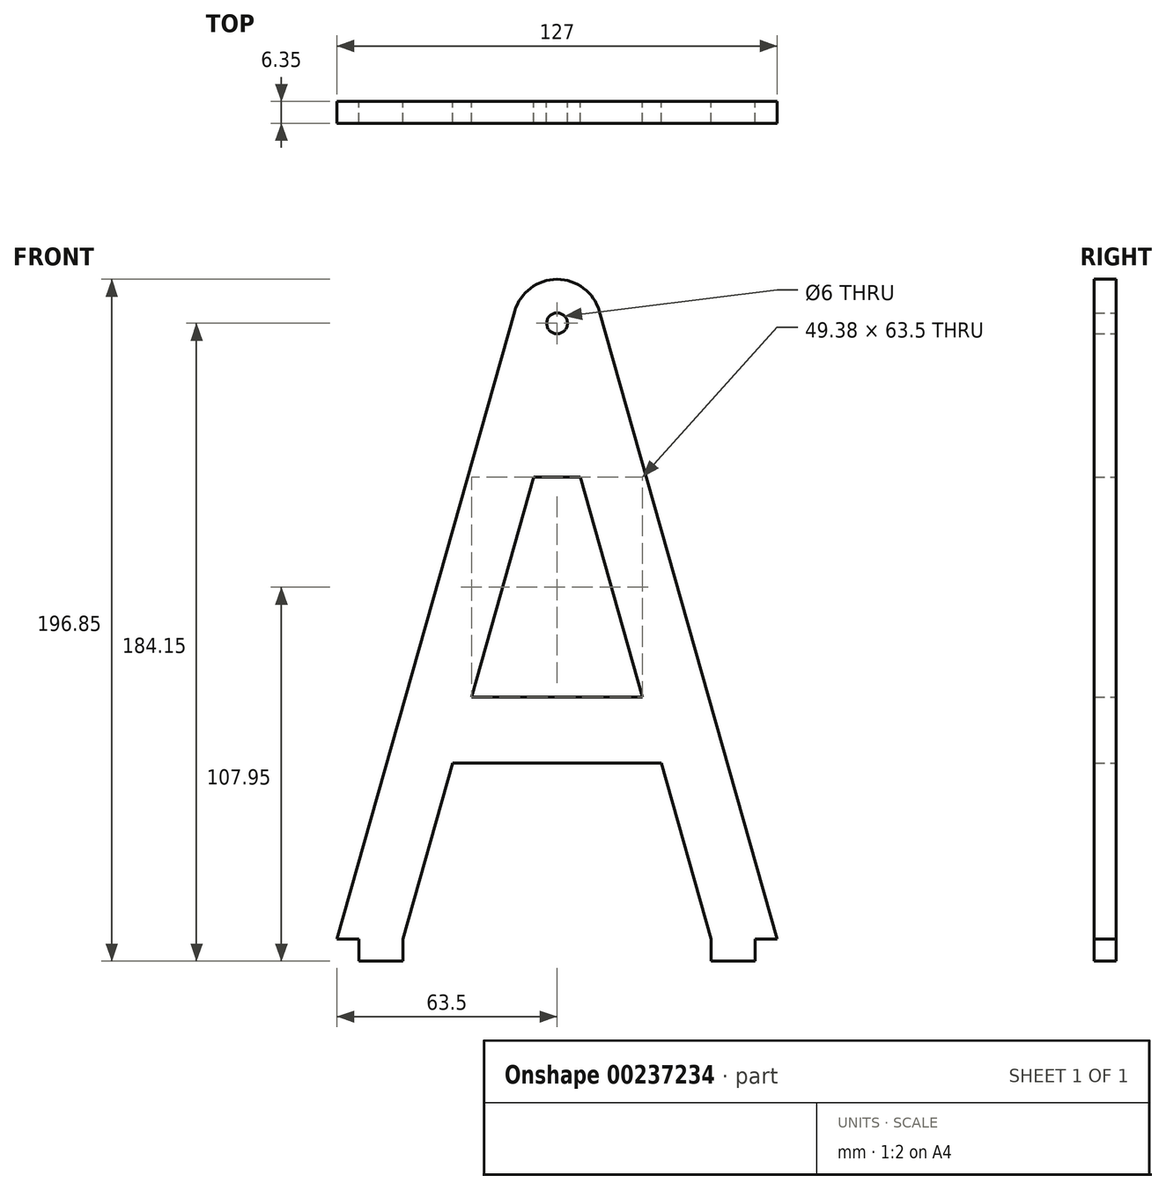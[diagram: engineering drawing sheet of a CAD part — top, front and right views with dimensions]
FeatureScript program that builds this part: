
annotation { "Feature Type Name" : "Feature", "Feature Type Description" : "" }
export const myFeature = defineFeature(function(context is Context, id is Id, definition is map)
    precondition{}
    {
        {
            var Q0;
            Q0=qCreatedBy(makeId("Front.planeOp"),FACE);
            var sketch = newSketch(context, id + "F0", { "sketchPlane" : qUnion([Q0])});
            skCircle(sketch, "E0", {"center": v(0, 177.8) * mm, "radius": 3 * mm});
            skArc(sketch, "E1", {"start": v(12.22, 181.26) * mm, "mid": v(0, 190.5) * mm, "end": v(-12.22, 181.26) * mm});
            skLineSegment(sketch, "E2", {"start": v(-12.22, 181.26) * mm, "end": v(-63.5, 0) * mm});
            skLineSegment(sketch, "E3", {"start": v(-63.5, 0) * mm, "end": v(-44.45, 0) * mm});
            skLineSegment(sketch, "E4", {"start": v(44.45, 0) * mm, "end": v(63.5, 0) * mm});
            skLineSegment(sketch, "E5", {"start": v(63.5, 0) * mm, "end": v(12.22, 181.26) * mm});
            skLineSegment(sketch, "E6", {"start": v(-30.08, 50.8) * mm, "end": v(30.08, 50.8) * mm});
            skLineSegment(sketch, "E7", {"start": v(30.08, 50.8) * mm, "end": v(44.45, 0) * mm});
            skLineSegment(sketch, "E8", {"start": v(-30.08, 50.8) * mm, "end": v(-44.45, 0) * mm});
            skLineSegment(sketch, "E9", {"start": v(-24.69, 69.85) * mm, "end": v(24.69, 69.85) * mm});
            skLineSegment(sketch, "E10", {"start": v(24.69, 69.85) * mm, "end": v(6.72, 133.35) * mm});
            skLineSegment(sketch, "E11", {"start": v(6.72, 133.35) * mm, "end": v(-6.72, 133.35) * mm});
            skLineSegment(sketch, "E12", {"start": v(-6.72, 133.35) * mm, "end": v(-24.69, 69.85) * mm});
            skSolve(sketch);
        }
        {
            var Q0;
            Q0 = qSketchRegion(id + "F0", true);
            extrude(context, id + "F1", {"entities" : qUnion([Q0]), "depth" : 6.35 * mm});
        }
        {
            var Q0;
            Q0=makeQuery(id+"F1.opExtrude","SWEPT_FACE",FACE,{"disambiguationData":[OSD([sQuery(id+"F0.wireOp",EDGE,"E3")])]});
            var sketch = newSketch(context, id + "F2", { "sketchPlane" : qUnion([Q0])});
            skLineSegment(sketch, "E13.bottom", {"start": v(-57.15, 6.35) * mm, "end": v(-44.45, 6.35) * mm});
            skLineSegment(sketch, "E13.top", {"start": v(-57.15, 0) * mm, "end": v(-44.45, 0) * mm});
            skLineSegment(sketch, "E13.left", {"start": v(-57.15, 6.35) * mm, "end": v(-57.15, 0) * mm});
            skLineSegment(sketch, "E13.right", {"start": v(-44.45, 6.35) * mm, "end": v(-44.45, 0) * mm});
            skLineSegment(sketch, "E14.bottom", {"start": v(44.45, 6.35) * mm, "end": v(57.15, 6.35) * mm});
            skLineSegment(sketch, "E14.top", {"start": v(44.45, 0) * mm, "end": v(57.15, 0) * mm});
            skLineSegment(sketch, "E14.left", {"start": v(44.45, 6.35) * mm, "end": v(44.45, 0) * mm});
            skLineSegment(sketch, "E14.right", {"start": v(57.15, 6.35) * mm, "end": v(57.15, 0) * mm});
            skSolve(sketch);
        }
        {
            var Q0;
            Q0 = qSketchRegion(id + "F2", true);
            extrude(context, id + "F3", {"entities" : qUnion([Q0]), "operationType" : NewBodyOperationType.ADD, "depth" : 6.35 * mm});
        }
    });
